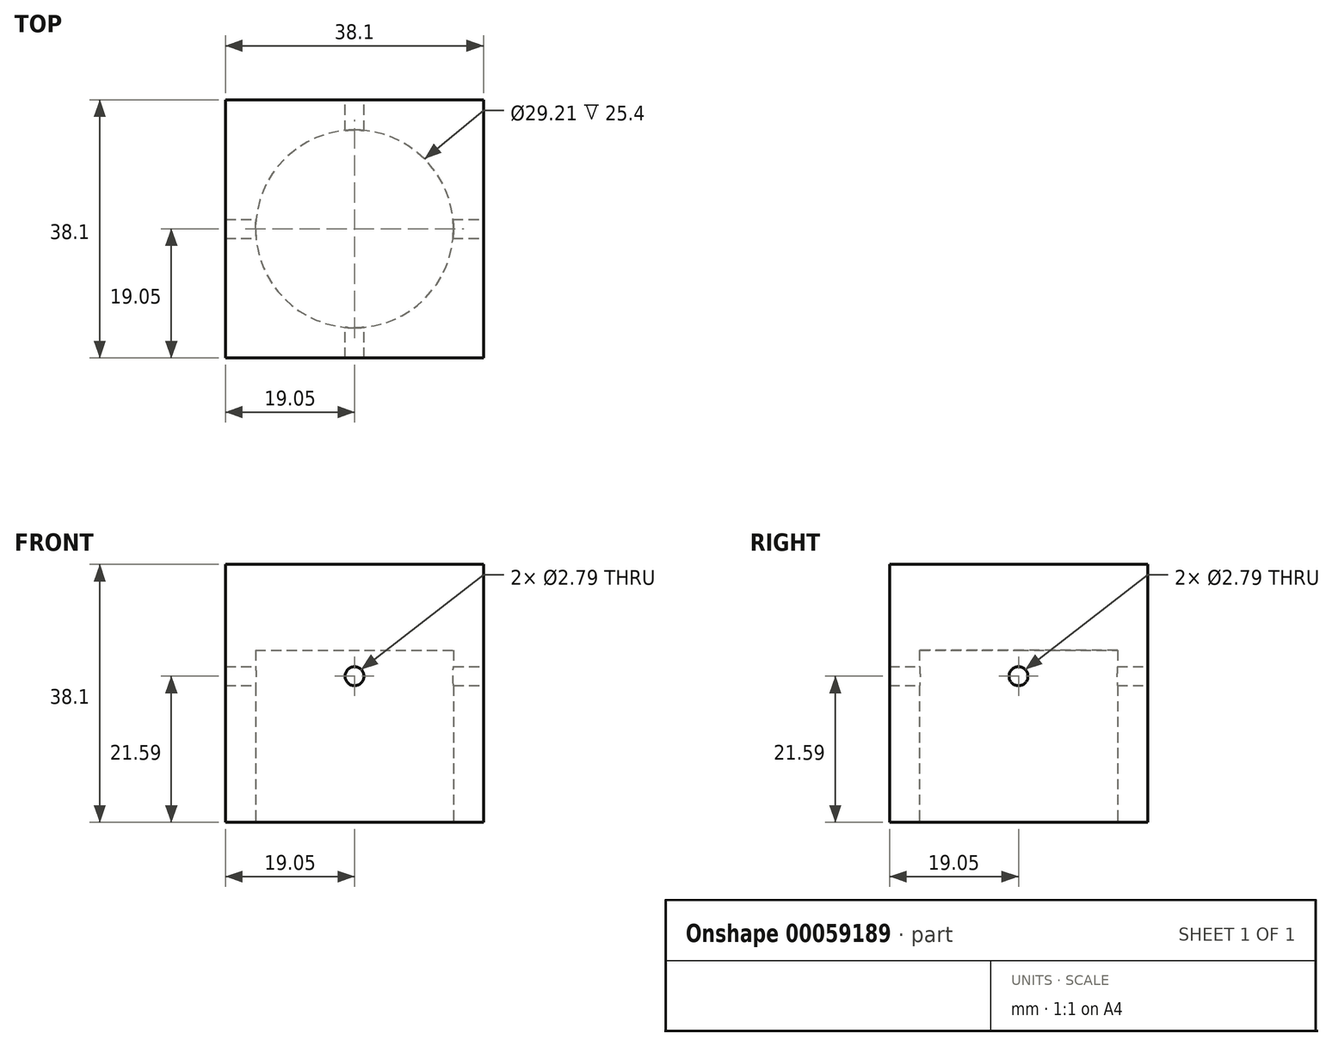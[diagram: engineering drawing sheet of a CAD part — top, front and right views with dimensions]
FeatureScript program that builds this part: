
annotation { "Feature Type Name" : "Feature", "Feature Type Description" : "" }
export const myFeature = defineFeature(function(context is Context, id is Id, definition is map)
    precondition{}
    {
        {
            var Q0;
            Q0=qCreatedBy(makeId("Top.planeOp"),FACE);
            var sketch = newSketch(context, id + "F0", { "sketchPlane" : qUnion([Q0])});
            skLineSegment(sketch, "E0.bottom", {"start": v(19.05, 19.05) * mm, "end": v(-19.05, 19.05) * mm});
            skLineSegment(sketch, "E0.top", {"start": v(19.05, -19.05) * mm, "end": v(-19.05, -19.05) * mm});
            skLineSegment(sketch, "E0.left", {"start": v(19.05, 19.05) * mm, "end": v(19.05, -19.05) * mm});
            skLineSegment(sketch, "E0.right", {"start": v(-19.05, 19.05) * mm, "end": v(-19.05, -19.05) * mm});
            skPoint(sketch, "E0.middle", {"position": v(0, 0) * mm});
            skSolve(sketch);
        }
        {
            var Q0;
            Q0=makeQuery(id+"F0.imprint","IMPRINT",FACE,{"disambiguationData":[TD([[makeQuery(id+"F0.imprint","IMPRINT",EDGE,{"derivedFrom":sQuery(id+"F0.wireOp",EDGE,"E0.bottom")}),1.0]])]});
            extrude(context, id + "F1", {"entities" : qUnion([Q0]), "depth" : 38.1 * mm});
        }
        {
            var Q0;
            Q0=makeQuery(id+"F1.opExtrude","CAP_FACE",FACE,{"disambiguationData":[OSD([sQuery(id+"F0.wireOp",EDGE,"E0.bottom"),sQuery(id+"F0.wireOp",EDGE,"E0.top"),sQuery(id+"F0.wireOp",EDGE,"E0.left"),sQuery(id+"F0.wireOp",EDGE,"E0.right")])],"isStart":true});
            var sketch = newSketch(context, id + "F2", { "sketchPlane" : qUnion([Q0])});
            skCircle(sketch, "E1", {"center": v(0, 0) * mm, "radius": 14.6 * mm});
            skSolve(sketch);
        }
        {
            var Q0;
            Q0=makeQuery(id+"F2.imprint","IMPRINT",FACE,{"disambiguationData":[TD([[makeQuery(id+"F2.imprint","IMPRINT",EDGE,{"derivedFrom":sQuery(id+"F2.wireOp",EDGE,"E1")}),1.0]])]});
            extrude(context, id + "F3", {"entities" : qUnion([Q0]), "operationType" : NewBodyOperationType.REMOVE, "oppositeDirection" : true, "depth" : 25.4 * mm});
        }
        {
            var Q0;
            Q0=makeQuery(id+"F1.opExtrude","SWEPT_FACE",FACE,{"disambiguationData":[OSD([sQuery(id+"F0.wireOp",EDGE,"E0.left")])]});
            var sketch = newSketch(context, id + "F4", { "sketchPlane" : qUnion([Q0])});
            skPoint(sketch, "E2", {"position": v(0, 21.59) * mm});
            skSolve(sketch);
        }
        {
            var Q0;
            Q0=sQuery(id+"F4.wireOp",VERTEX,"E2");
            var Q1;
            Q1=makeQuery(id+"F1.opExtrude","SWEPT_BODY",BODY,{"disambiguationData":[OSD([sQuery(id+"F0.wireOp",EDGE,"E0.bottom"),sQuery(id+"F0.wireOp",EDGE,"E0.top"),sQuery(id+"F0.wireOp",EDGE,"E0.left"),sQuery(id+"F0.wireOp",EDGE,"E0.right")])]});
            hole(context, id + "F5", {"style" : HoleStyle.SIMPLE, "endStyle" : HoleEndStyle.THROUGH, "holeDiameter" : 2.8 * mm, "locations" : qUnion([Q0]), "scope" : qUnion([Q1]), "isTappedThrough" : true});
        }
        {
            var Q0;
            Q0=makeQuery(id+"F1.opExtrude","SWEPT_FACE",FACE,{"disambiguationData":[OSD([sQuery(id+"F0.wireOp",EDGE,"E0.bottom")])]});
            var sketch = newSketch(context, id + "F6", { "sketchPlane" : qUnion([Q0])});
            skPoint(sketch, "E3", {"position": v(0, 21.59) * mm});
            skSolve(sketch);
        }
        {
            var Q0;
            Q0=sQuery(id+"F6.wireOp",VERTEX,"E3");
            var Q1;
            Q1=makeQuery(id+"F1.opExtrude","SWEPT_BODY",BODY,{"disambiguationData":[OSD([sQuery(id+"F0.wireOp",EDGE,"E0.bottom"),sQuery(id+"F0.wireOp",EDGE,"E0.top"),sQuery(id+"F0.wireOp",EDGE,"E0.left"),sQuery(id+"F0.wireOp",EDGE,"E0.right")])]});
            hole(context, id + "F7", {"style" : HoleStyle.SIMPLE, "endStyle" : HoleEndStyle.THROUGH, "holeDiameter" : 2.8 * mm, "locations" : qUnion([Q0]), "scope" : qUnion([Q1]), "isTappedThrough" : true});
        }
    });
